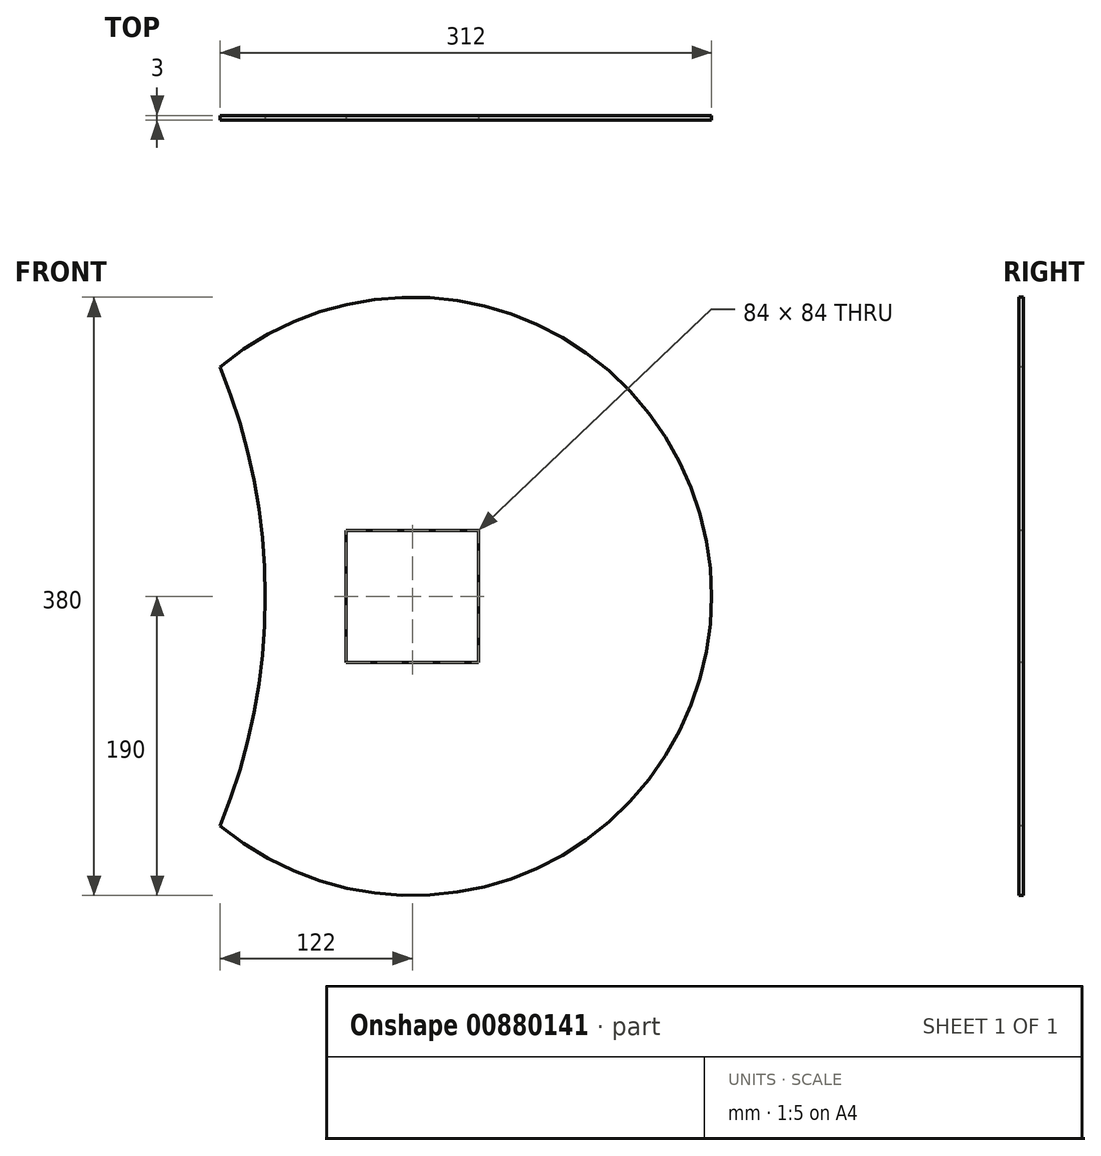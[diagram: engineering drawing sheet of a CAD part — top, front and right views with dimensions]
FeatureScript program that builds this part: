
annotation { "Feature Type Name" : "Feature", "Feature Type Description" : "" }
export const myFeature = defineFeature(function(context is Context, id is Id, definition is map)
    precondition{}
    {
        {
            var Q0;
            Q0=qCreatedBy(makeId("Front.planeOp"),FACE);
            var sketch = newSketch(context, id + "F0", { "sketchPlane" : qUnion([Q0])});
            skCircle(sketch, "E0", {"center": v(0, 0) * mm, "radius": 190 * mm});
            skSolve(sketch);
        }
        {
            var Q0;
            Q0 = qSketchRegion(id + "F0", true);
            extrude(context, id + "F1", {"entities" : qUnion([Q0]), "depth" : 3 * mm, "offsetDistance" : 25 * mm});
        }
        {
            var Q0;
            Q0=makeQuery(id+"F1.opExtrude","CAP_FACE",FACE,{"disambiguationData":[OSD([sQuery(id+"F0.wireOp",EDGE,"E0")])],"isStart":false});
            var sketch = newSketch(context, id + "F2", { "sketchPlane" : qUnion([Q0])});
            skLineSegment(sketch, "E1.bottom", {"start": v(0, 0) * mm, "end": v(42, 0) * mm});
            skLineSegment(sketch, "E1.top", {"start": v(0, -42) * mm, "end": v(42, -42) * mm});
            skLineSegment(sketch, "E1.left", {"start": v(0, 0) * mm, "end": v(0, -42) * mm});
            skLineSegment(sketch, "E1.right", {"start": v(42, 0) * mm, "end": v(42, -42) * mm});
            skLineSegment(sketch, "E2.bottom", {"start": v(0, 0) * mm, "end": v(-42, 0) * mm});
            skLineSegment(sketch, "E2.top", {"start": v(0, -42) * mm, "end": v(-42, -42) * mm});
            skLineSegment(sketch, "E2.right", {"start": v(-42, 0) * mm, "end": v(-42, -42) * mm});
            skLineSegment(sketch, "E3.top", {"start": v(0, 42) * mm, "end": v(-42, 42) * mm});
            skLineSegment(sketch, "E3.left", {"start": v(0, 0) * mm, "end": v(0, 42) * mm});
            skLineSegment(sketch, "E3.right", {"start": v(-42, 0) * mm, "end": v(-42, 42) * mm});
            skLineSegment(sketch, "E4", {"start": v(0, 42) * mm, "end": v(42, 42) * mm});
            skLineSegment(sketch, "E5", {"start": v(42, 42) * mm, "end": v(42, 0) * mm});
            skSolve(sketch);
        }
        {
            var Q0;
            Q0=makeQuery(id+"F2.imprint","IMPRINT",FACE,{"disambiguationData":[TD([[makeQuery(id+"F2.imprint","IMPRINT",EDGE,{"derivedFrom":sQuery(id+"F2.wireOp",EDGE,"E1.left")}),-1.0]])]});
            var Q1;
            Q1=makeQuery(id+"F2.imprint","IMPRINT",FACE,{"disambiguationData":[TD([[makeQuery(id+"F2.imprint","IMPRINT",EDGE,{"derivedFrom":sQuery(id+"F2.wireOp",EDGE,"E1.bottom")}),-1.0]])]});
            var Q2;
            Q2=makeQuery(id+"F2.imprint","IMPRINT",FACE,{"disambiguationData":[TD([[makeQuery(id+"F2.imprint","IMPRINT",EDGE,{"derivedFrom":sQuery(id+"F2.wireOp",EDGE,"E1.bottom")}),1.0]])]});
            var Q3;
            Q3=makeQuery(id+"F2.imprint","IMPRINT",FACE,{"disambiguationData":[TD([[makeQuery(id+"F2.imprint","IMPRINT",EDGE,{"derivedFrom":sQuery(id+"F2.wireOp",EDGE,"E2.bottom")}),-1.0]])]});
            extrude(context, id + "F3", {"entities" : qUnion([Q0, Q1, Q2, Q3]), "operationType" : NewBodyOperationType.REMOVE, "endBound" : BoundingType.THROUGH_ALL, "oppositeDirection" : true, "depth" : 25 * mm, "offsetDistance" : 25 * mm});
        }
        {
            var Q0;
            Q0=makeQuery(id+"F1.opExtrude","CAP_FACE",FACE,{"disambiguationData":[OSD([sQuery(id+"F0.wireOp",EDGE,"E0")])],"isStart":false});
            var sketch = newSketch(context, id + "F4", { "sketchPlane" : qUnion([Q0])});
            skLineSegment(sketch, "E6", {"start": v(-42, 0) * mm, "end": v(-122, 0) * mm});
            skLineSegment(sketch, "E7", {"start": v(-122, 0) * mm, "end": v(-122, 145.66) * mm});
            skLineSegment(sketch, "E8", {"start": v(-122, 145.66) * mm, "end": v(-122, -145.66) * mm});
            skArc(sketch, "E9", {"start": v(-122, -145.66) * mm, "mid": v(-93.5, 0) * mm, "end": v(-122, 145.66) * mm});
            skSolve(sketch);
        }
        {
            var Q0;
            Q0 = qSketchRegion(id + "F4", true);
            var Q1;
            {var subQ0=sQuery(id+"F4.wireOp",EDGE,"E7");Q1=makeQuery(id+"F4.imprint","IMPRINT",FACE,{"disambiguationData":[TD([[makeQuery(id+"F4.imprint","IMPRINT",EDGE,{"derivedFrom":subQ0}),1.0]])]});}
            extrude(context, id + "F5", {"entities" : qUnion([Q0, Q1]), "operationType" : NewBodyOperationType.REMOVE, "endBound" : BoundingType.THROUGH_ALL, "oppositeDirection" : true, "depth" : 25 * mm, "offsetDistance" : 25 * mm});
        }
    });
